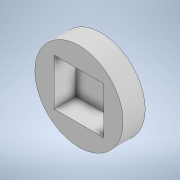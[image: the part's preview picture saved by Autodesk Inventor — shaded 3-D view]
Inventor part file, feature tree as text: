
AUTODESK INVENTOR PART (.ipt)
format: ipt  version: 2021 (Build 250183000, 183)  size: 354,304 bytes
history: native  units: in
note: dims shown in document units (in); Inventor stores cm internally (conversion verified against a paired STEP export)
features: sketch x6, extrude x5, projected_geometry x4, pattern_linear x2, plane x1, mirror x1
ambient origin geometry x8: Origin, YZ Plane, XZ Plane, XY Plane, X Axis, Y Axis, Z Axis, Center Point
bodies: Body1 (feature_tree)
feature tree (19):
  sketch  "Sketch1"  dims[d0=1.1295in d1=1.06in]
  plane  "Work Plane1"
  extrude  "Extrusion2"  Depth=1.06in
  extrude  "Extrusion3"  Depth=0.5in TaperAngle=0.0deg
  extrude  "Extrusion4"  Depth=0.006in TaperAngle=0.0deg
  pattern_linear  "Rectangular Pattern1"  Count1=12 Spacing1=0.1in
  extrude  "Extrusion5"  Depth=0.006in TaperAngle=0.0deg
  extrude  "Extrusion6"  TaperAngle=0.0deg  [1 undecoded]
  pattern_linear  "Rectangular Pattern2"  Count1=6 Spacing1=0.2in
  mirror  "Mirror1"
  sketch  "Sketch6"
  sketch  "Sketch2"  dims[d4=2.0in d5=0.5in d6=0.0in]
  sketch  "Sketch3"  dims[d7=0.25in d8=0.0in d10=0.006in d11=0.0in d12=4.7244in d14=0.1in]
  projected_geometry  "Projected Loop1"
  projected_geometry  "Projected Loop2"
  sketch  "Sketch4"  dims[d15=0.01in d16=0.006in d17=0.0in]
  projected_geometry  "Projected Loop3"
  sketch  "Sketch5"  dims[d18=0.0394in d20=0.0in d21=0.0in d22=2.3622in d24=0.2in]
  projected_geometry  "Projected Loop4"
note: 1 required parameter value undecoded (feature->parameter linkage not recoverable at this tier; creation-order binding heuristic only, values carry confidence <= 0.55)
